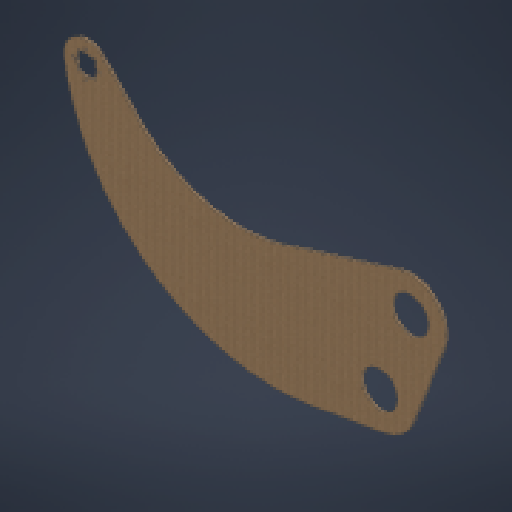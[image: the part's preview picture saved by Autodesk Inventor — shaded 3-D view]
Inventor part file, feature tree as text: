
AUTODESK INVENTOR PART (.ipt)
format: ipt  version: 2024.1 (Build 281209000, 209)  size: 208,384 bytes
history: native  units: in
note: dims shown in document units (in); Inventor stores cm internally (conversion verified against a paired STEP export)
features: extrude x1, fillet x1, sketch x1
ambient origin geometry x8: Origin, YZ Plane, XZ Plane, XY Plane, X Axis, Y Axis, Z Axis, Center Point
bodies: Solid1 (feature_tree)
feature tree (3):
  extrude  "Extrusion1"  Depth=12.0in
  fillet  "Fillet1"  Radius=0.1202in
  sketch  "Sketch1"  dims[d0=6.0in d1=12.0in d2=0.1202in d3=4.0in d4=4.0in d5=4.8in d6=0.7627in d7=24.0in d9=1.1681in d10=0.1575in d11=0.1575in d12=0.1575in d13=0.1575in d14=0.125in d15=0.0in d16=2.0in d17=2.0in d18=8.0in d19=0.0in d20=0.0in d21=0.0in]
